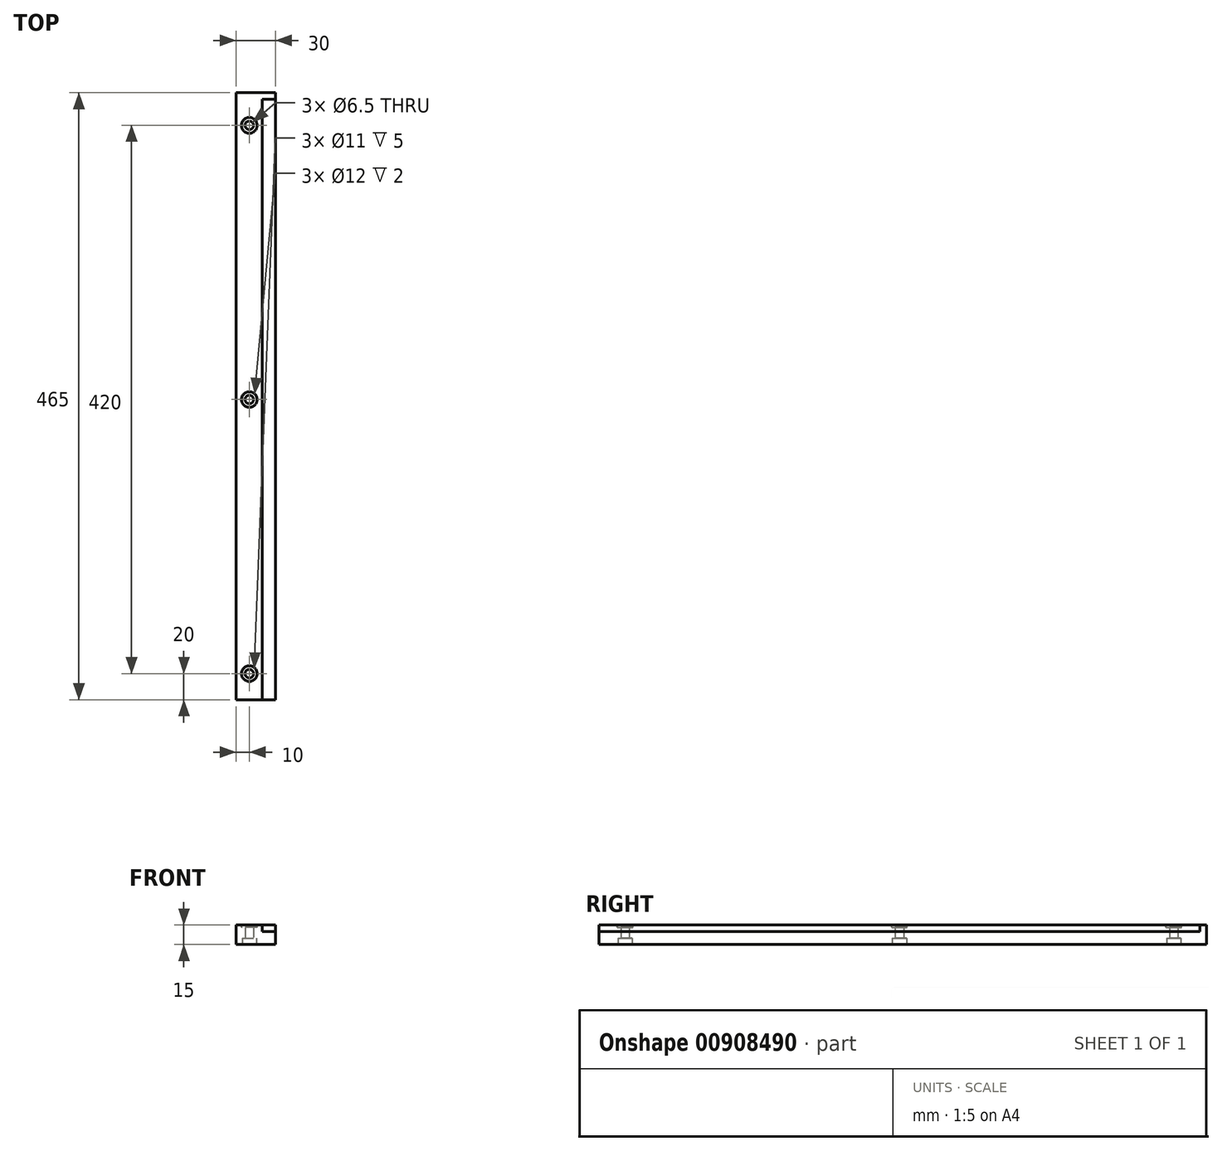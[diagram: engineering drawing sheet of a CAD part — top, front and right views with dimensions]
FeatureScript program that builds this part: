
annotation { "Feature Type Name" : "Feature", "Feature Type Description" : "" }
export const myFeature = defineFeature(function(context is Context, id is Id, definition is map)
    precondition{}
    {
        {
            var Q0;
            Q0=qCreatedBy(makeId("Front.planeOp"),FACE);
            var sketch = newSketch(context, id + "F0", { "sketchPlane" : qUnion([Q0])});
            skLineSegment(sketch, "E0.bottom", {"start": v(0, 0) * mm, "end": v(30, 0) * mm});
            skLineSegment(sketch, "E0.top", {"start": v(0, 15) * mm, "end": v(20, 15) * mm});
            skLineSegment(sketch, "E0.left", {"start": v(0, 0) * mm, "end": v(0, 15) * mm});
            skLineSegment(sketch, "E0.right", {"start": v(30, 0) * mm, "end": v(30, 10) * mm});
            skLineSegment(sketch, "E1.top", {"start": v(30, 10) * mm, "end": v(20, 10) * mm});
            skLineSegment(sketch, "E1.right", {"start": v(20, 15) * mm, "end": v(20, 10) * mm});
            skSolve(sketch);
        }
        {
            var Q0;
            Q0=makeQuery(id+"F0.imprint","IMPRINT",FACE,{"disambiguationData":[TD([[makeQuery(id+"F0.imprint","IMPRINT",EDGE,{"derivedFrom":sQuery(id+"F0.wireOp",EDGE,"E0.bottom")}),1.0]])]});
            extrude(context, id + "F1", {"entities" : qUnion([Q0]), "oppositeDirection" : true, "depth" : 460 * mm, "offsetDistance" : 25 * mm});
        }
        {
            var Q0;
            Q0=makeQuery(id+"F1.opExtrude","SWEPT_FACE",FACE,{"disambiguationData":[OSD([sQuery(id+"F0.wireOp",EDGE,"E0.bottom")])]});
            var sketch = newSketch(context, id + "F2", { "sketchPlane" : qUnion([Q0])});
            skCircle(sketch, "E2", {"center": v(10, -20) * mm, "radius": 2.5 * mm});
            skCircle(sketch, "E3", {"center": v(10, -230) * mm, "radius": 2.5 * mm});
            skCircle(sketch, "E4", {"center": v(10, -440) * mm, "radius": 2.5 * mm});
            skSolve(sketch);
        }
        {
            var Q0;
            Q0=sQuery(id+"F2.wireOp",VERTEX,"E4.center");
            var Q1;
            Q1=sQuery(id+"F2.wireOp",VERTEX,"E3.center");
            var Q2;
            Q2=sQuery(id+"F2.wireOp",VERTEX,"E2.center");
            var Q3;
            Q3=makeQuery(id+"F1.opExtrude","SWEPT_BODY",BODY,{"disambiguationData":[OSD([sQuery(id+"F0.wireOp",EDGE,"E0.bottom"),sQuery(id+"F0.wireOp",EDGE,"E0.top"),sQuery(id+"F0.wireOp",EDGE,"E0.left"),sQuery(id+"F0.wireOp",EDGE,"E0.right"),sQuery(id+"F0.wireOp",EDGE,"E1.top"),sQuery(id+"F0.wireOp",EDGE,"E1.right")])]});
            hole(context, id + "F3", {"style" : HoleStyle.C_BORE, "endStyle" : HoleEndStyle.BLIND, "holeDiameter" : 6.5 * mm, "cBoreDiameter" : 11 * mm, "cBoreDepth" : 5 * mm, "majorDiameter" : 5 * mm, "holeDepth" : 15 * mm, "isTappedThrough" : true, "tappedDepth" : 12 * mm, "tapClearance" : 3, "locations" : qUnion([Q0, Q1, Q2]), "scope" : qUnion([Q3])});
        }
        {
            var Q0;
            Q0=makeQuery(id+"F1.opExtrude","SWEPT_FACE",FACE,{"disambiguationData":[OSD([sQuery(id+"F0.wireOp",EDGE,"E0.top")])]});
            var sketch = newSketch(context, id + "F4", { "sketchPlane" : qUnion([Q0])});
            skCircle(sketch, "E5", {"center": v(10, 20) * mm, "radius": 5 * mm});
            skCircle(sketch, "E6", {"center": v(10, 230) * mm, "radius": 5 * mm});
            skCircle(sketch, "E7", {"center": v(10, 440) * mm, "radius": 5 * mm});
            skSolve(sketch);
        }
        {
            var Q0;
            Q0=sQuery(id+"F4.wireOp",VERTEX,"E7.center");
            var Q1;
            Q1=sQuery(id+"F4.wireOp",VERTEX,"E6.center");
            var Q2;
            Q2=sQuery(id+"F4.wireOp",VERTEX,"E5.center");
            var Q3;
            Q3=makeQuery(id+"F1.opExtrude","SWEPT_BODY",BODY,{"disambiguationData":[OSD([sQuery(id+"F0.wireOp",EDGE,"E0.bottom"),sQuery(id+"F0.wireOp",EDGE,"E0.top"),sQuery(id+"F0.wireOp",EDGE,"E0.left"),sQuery(id+"F0.wireOp",EDGE,"E0.right"),sQuery(id+"F0.wireOp",EDGE,"E1.top"),sQuery(id+"F0.wireOp",EDGE,"E1.right")])]});
            hole(context, id + "F5", {"style" : HoleStyle.C_BORE, "endStyle" : HoleEndStyle.BLIND, "holeDiameter" : 6.5 * mm, "cBoreDiameter" : 12 * mm, "cBoreDepth" : 2 * mm, "majorDiameter" : 5 * mm, "holeDepth" : 15 * mm, "isTappedThrough" : true, "tappedDepth" : 12 * mm, "tapClearance" : 3, "locations" : qUnion([Q0, Q1, Q2]), "scope" : qUnion([Q3])});
        }
        {
            var Q0;
            Q0=makeQuery(id+"F1.opExtrude","CAP_FACE",FACE,{"disambiguationData":[OSD([sQuery(id+"F0.wireOp",EDGE,"E0.bottom"),sQuery(id+"F0.wireOp",EDGE,"E0.top"),sQuery(id+"F0.wireOp",EDGE,"E0.left"),sQuery(id+"F0.wireOp",EDGE,"E0.right"),sQuery(id+"F0.wireOp",EDGE,"E1.top"),sQuery(id+"F0.wireOp",EDGE,"E1.right")])],"isStart":false});
            var sketch = newSketch(context, id + "F6", { "sketchPlane" : qUnion([Q0])});
            skPoint(sketch, "E8.oppositeSnap0", {"position": v(-10, 15) * mm});
            skLineSegment(sketch, "E8.bottom", {"start": v(0, 0) * mm, "end": v(-30, 0) * mm});
            skLineSegment(sketch, "E8.top", {"start": v(0, 15) * mm, "end": v(-30, 15) * mm});
            skLineSegment(sketch, "E8.left", {"start": v(0, 0) * mm, "end": v(0, 15) * mm});
            skLineSegment(sketch, "E8.right", {"start": v(-30, 0) * mm, "end": v(-30, 15) * mm});
            skSolve(sketch);
        }
        {
            var Q0;
            Q0 = qSketchRegion(id + "F6", true);
            extrude(context, id + "F7", {"entities" : qUnion([Q0]), "operationType" : NewBodyOperationType.ADD, "depth" : 5 * mm, "offsetDistance" : 25 * mm});
        }
    });
